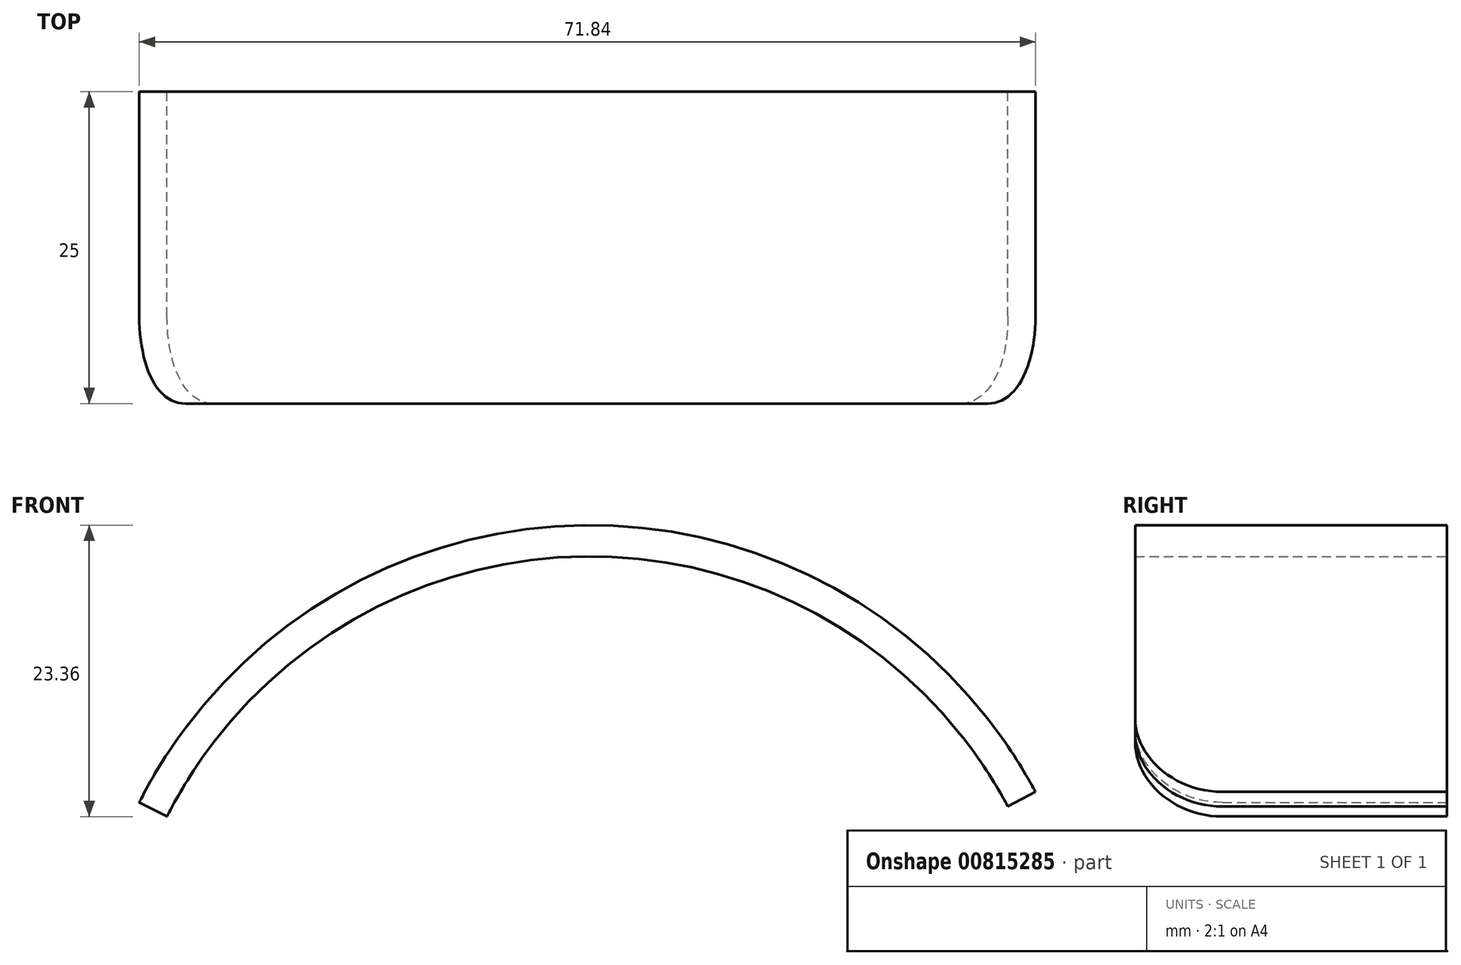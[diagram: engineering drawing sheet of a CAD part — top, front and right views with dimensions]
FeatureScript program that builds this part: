
annotation { "Feature Type Name" : "Feature", "Feature Type Description" : "" }
export const myFeature = defineFeature(function(context is Context, id is Id, definition is map)
    precondition{}
    {
        {
            var Q0;
            Q0=qCreatedBy(makeId("Front.planeOp"),FACE);
            var sketch = newSketch(context, id + "F0", { "sketchPlane" : qUnion([Q0])});
            skArc(sketch, "E0", {"start": v(33.5, 17.95) * mm, "mid": v(-0.45, 38) * mm, "end": v(-33.91, 17.14) * mm});
            skLineSegment(sketch, "E1", {"start": v(0, 0) * mm, "end": v(-33.91, 17.14) * mm, "construction": true});
            skLineSegment(sketch, "E2", {"start": v(0, 0) * mm, "end": v(33.5, 17.95) * mm, "construction": true});
            skLineSegment(sketch, "E3", {"start": v(-33.91, 17.14) * mm, "end": v(-36.14, 18.27) * mm});
            skLineSegment(sketch, "E4", {"start": v(33.5, 17.95) * mm, "end": v(35.7, 19.13) * mm});
            skArc(sketch, "E5", {"start": v(35.7, 19.13) * mm, "mid": v(-0.48, 40.5) * mm, "end": v(-36.14, 18.27) * mm});
            skSolve(sketch);
        }
        {
            var Q0;
            Q0=makeQuery(id+"F0.imprint","IMPRINT",FACE,{"disambiguationData":[TD([[makeQuery(id+"F0.imprint","IMPRINT",EDGE,{"derivedFrom":sQuery(id+"F0.wireOp",EDGE,"E0")}),-1.0]])]});
            extrude(context, id + "F1", {"entities" : qUnion([Q0]), "depth" : 25 * mm, "offsetDistance" : 25 * mm, "symmetric" : true});
        }
        {
            var Q0;
            Q0=makeQuery(id+"F1.opExtrude","CAP_EDGE",EDGE,{"disambiguationData":[OSD([sQuery(id+"F0.wireOp",EDGE,"E4")])],"isStart":false});
            var Q1;
            Q1=makeQuery(id+"F1.opExtrude","CAP_EDGE",EDGE,{"disambiguationData":[OSD([sQuery(id+"F0.wireOp",EDGE,"E3")])],"isStart":false});
            fillet(context, id + "F2", {"entities" : qUnion([Q0, Q1]), "radius" : 7 * mm, "tangentPropagation" : true, "allowEdgeOverflow" : false});
        }
    });
